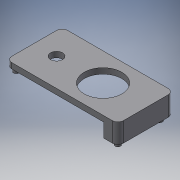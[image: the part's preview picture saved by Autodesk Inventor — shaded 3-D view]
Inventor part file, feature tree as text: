
AUTODESK INVENTOR PART (.ipt)
format: ipt  version: 2019 (Build 230136000, 136)  size: 158,208 bytes
history: native  units: mm
features: sketch x6, extrude x5, other x3, reference x2, fillet x1, hole x1
ambient origin geometry x8: Origin, YZ Plane, XZ Plane, XY Plane, X Axis, Y Axis, Z Axis, Center Point
bodies: Solid1 (feature_tree)
feature tree (18):
  extrude  "Extrusion1"  Depth=40.0mm
  extrude  "Extrusion4"  Depth=2.0mm TaperAngle=0.0deg
  extrude  "Extrusion3"  Depth=2.0mm
  extrude  "Extrusion5"  Depth=5.0mm
  fillet  "Fillet1"  Radius=1.9mm
  extrude  "Extrusion6"  Depth=2.5mm
  hole  "Hole1"  [1 undecoded]
  sketch  "Sketch1"  dims[d0=2.0mm d1=0.0mm d2=40.0mm]
  sketch  "Sketch4"  dims[d3=20.0mm d12=2.0mm d13=0.0mm]
  sketch  "Sketch5"  dims[d15=5.0mm d16=0.0mm d24=2.0mm]
  sketch  "Sketch6"  dims[d25=5.0mm d26=1.9mm d27=1.9mm]
  sketch  "Sketch7"  dims[d28=2.5mm d29=2.5mm]
  reference  "Reference1"
  sketch  "Sketch8"  dims[d30=2.5mm d31=1.9mm d32=1.9mm d33=1.5mm d34=2.0mm d35=2.0mm d36=2.0mm d37=0.0mm d38=13.5mm d39=2.0mm d40=0.0mm d41=4.305mm d42=6.0mm d43=7.087mm d44=2.0mm d45=14.3117mm d46=8.0mm d47=20.594885mm]
  reference  "Reference2"
  other  "<userpath>\Documents\IQC\CameraSetup.iam"
  other  "CameraSetup.iam"
  other  "PinionHolder:1"
note: 1 required parameter value undecoded (feature->parameter linkage not recoverable at this tier; creation-order binding heuristic only, values carry confidence <= 0.55)
